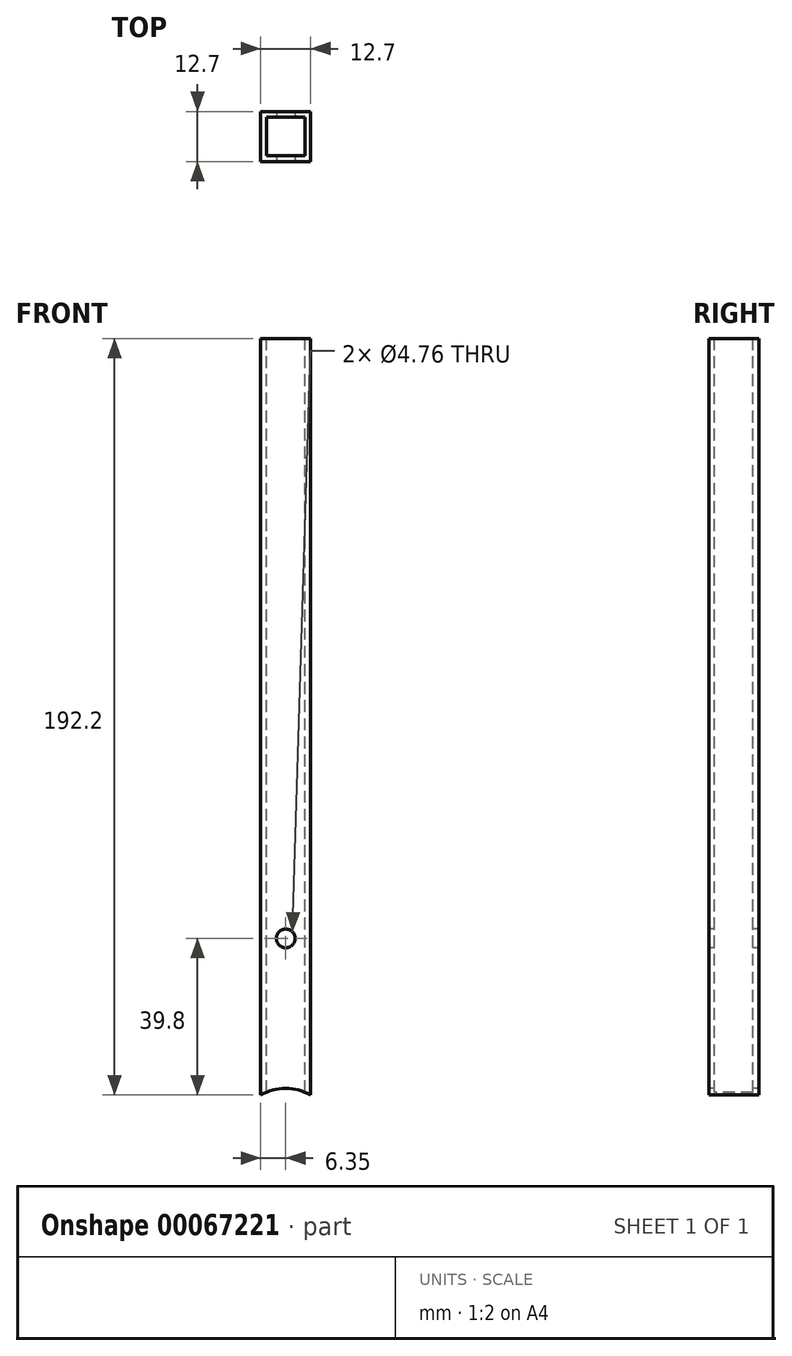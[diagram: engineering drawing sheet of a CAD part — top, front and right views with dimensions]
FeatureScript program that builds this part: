
annotation { "Feature Type Name" : "Feature", "Feature Type Description" : "" }
export const myFeature = defineFeature(function(context is Context, id is Id, definition is map)
    precondition{}
    {
        {
            var Q0;
            Q0=qCreatedBy(makeId("Top.planeOp"),FACE);
            var sketch = newSketch(context, id + "F0", { "sketchPlane" : qUnion([Q0])});
            skLineSegment(sketch, "E0.bottom", {"start": v(0, 0) * mm, "end": v(12.7, 0) * mm});
            skLineSegment(sketch, "E0.top", {"start": v(0, 12.7) * mm, "end": v(12.7, 12.7) * mm});
            skLineSegment(sketch, "E0.left", {"start": v(0, 0) * mm, "end": v(0, 12.7) * mm});
            skLineSegment(sketch, "E0.right", {"start": v(12.7, 0) * mm, "end": v(12.7, 12.7) * mm});
            skSolve(sketch);
        }
        {
            var Q0;
            Q0=makeQuery(id+"F0.imprint","IMPRINT",FACE,{"disambiguationData":[TD([[makeQuery(id+"F0.imprint","IMPRINT",EDGE,{"derivedFrom":sQuery(id+"F0.wireOp",EDGE,"E0.bottom")}),1.0]])]});
            extrude(context, id + "F1", {"entities" : qUnion([Q0]), "depth" : 203.2 * mm});
        }
        {
            var Q0;
            Q0=makeQuery(id+"F1.opExtrude","SWEPT_FACE",FACE,{"disambiguationData":[OSD([sQuery(id+"F0.wireOp",EDGE,"E0.bottom")])]});
            var sketch = newSketch(context, id + "F2", { "sketchPlane" : qUnion([Q0])});
            skCircle(sketch, "E1", {"center": v(6.35, 0) * mm, "radius": 12.7 * mm});
            skSolve(sketch);
        }
        {
            var Q0;
            {var subQ1=sQuery(id+"F0.wireOp",EDGE,"E0.bottom");var subQ6=makeQuery(id+"F1.opExtrude","CAP_EDGE",EDGE,{"disambiguationData":[OSD([subQ1])],"isStart":true});Q0=makeQuery(id+"F2.imprint","IMPRINT",FACE,{"disambiguationData":[TD([[makeQuery(id+"F2.imprint","IMPRINT",EDGE,{"derivedFrom":subQ6}),-1.0]])]});}
            var Q1;
            {var subQ1=sQuery(id+"F0.wireOp",EDGE,"E0.bottom");var subQ6=makeQuery(id+"F1.opExtrude","CAP_EDGE",EDGE,{"disambiguationData":[OSD([subQ1])],"isStart":true});Q1=makeQuery(id+"F2.imprint","IMPRINT",FACE,{"disambiguationData":[TD([[makeQuery(id+"F2.imprint","IMPRINT",EDGE,{"derivedFrom":subQ6}),1.0]])]});}
            extrude(context, id + "F3", {"entities" : qUnion([Q0, Q1]), "operationType" : NewBodyOperationType.REMOVE, "oppositeDirection" : true, "depth" : 25.4 * mm});
        }
        {
            var Q0;
            Q0=makeQuery(id+"F1.opExtrude","CAP_FACE",FACE,{"disambiguationData":[OSD([sQuery(id+"F0.wireOp",EDGE,"E0.bottom"),sQuery(id+"F0.wireOp",EDGE,"E0.top"),sQuery(id+"F0.wireOp",EDGE,"E0.left"),sQuery(id+"F0.wireOp",EDGE,"E0.right")])],"isStart":false});
            var sketch = newSketch(context, id + "F4", { "sketchPlane" : qUnion([Q0])});
            skLineSegment(sketch, "E2.0", {"start": v(0, 12.7) * mm, "end": v(12.7, 12.7) * mm});
            skLineSegment(sketch, "E3.0", {"start": v(12.7, 0) * mm, "end": v(12.7, 12.7) * mm});
            skLineSegment(sketch, "E4.0", {"start": v(0, 0) * mm, "end": v(0, 12.7) * mm});
            skLineSegment(sketch, "E5.0", {"start": v(0, 0) * mm, "end": v(12.7, 0) * mm});
            skLineSegment(sketch, "E6.bottom", {"start": v(1.45, 1.45) * mm, "end": v(11.25, 1.45) * mm});
            skLineSegment(sketch, "E6.top", {"start": v(1.45, 11.25) * mm, "end": v(11.25, 11.25) * mm});
            skLineSegment(sketch, "E6.left", {"start": v(1.45, 1.45) * mm, "end": v(1.45, 11.25) * mm});
            skLineSegment(sketch, "E6.right", {"start": v(11.25, 1.45) * mm, "end": v(11.25, 11.25) * mm});
            skLineSegment(sketch, "E7", {"start": v(1.45, 11.25) * mm, "end": v(11.25, 1.45) * mm, "construction": true});
            skLineSegment(sketch, "E8", {"start": v(11.25, 11.25) * mm, "end": v(1.45, 1.45) * mm, "construction": true});
            skPoint(sketch, "E9", {"position": v(6.35, 6.35) * mm});
            skLineSegment(sketch, "E10", {"start": v(0, 12.7) * mm, "end": v(12.7, 0) * mm, "construction": true});
            skLineSegment(sketch, "E11", {"start": v(0, 0) * mm, "end": v(12.7, 12.7) * mm, "construction": true});
            skSolve(sketch);
        }
        {
            var Q0;
            Q0=makeQuery(id+"F4.imprint","IMPRINT",FACE,{"disambiguationData":[TD([[makeQuery(id+"F4.imprint","IMPRINT",EDGE,{"derivedFrom":sQuery(id+"F4.wireOp",EDGE,"E6.bottom")}),1.0]])]});
            extrude(context, id + "F5", {"entities" : qUnion([Q0]), "operationType" : NewBodyOperationType.REMOVE, "oppositeDirection" : true, "depth" : 254 * mm});
        }
        {
            var Q0;
            Q0=makeQuery(id+"F1.opExtrude","SWEPT_FACE",FACE,{"disambiguationData":[OSD([sQuery(id+"F0.wireOp",EDGE,"E0.bottom")])]});
            var sketch = newSketch(context, id + "F6", { "sketchPlane" : qUnion([Q0])});
            skCircle(sketch, "E12", {"center": v(6.35, 50.8) * mm, "radius": 2.38 * mm});
            skSolve(sketch);
        }
        {
            var Q0;
            Q0=makeQuery(id+"F6.imprint","IMPRINT",FACE,{"disambiguationData":[TD([[makeQuery(id+"F6.imprint","IMPRINT",EDGE,{"derivedFrom":sQuery(id+"F6.wireOp",EDGE,"E12")}),1.0]])]});
            extrude(context, id + "F7", {"entities" : qUnion([Q0]), "operationType" : NewBodyOperationType.REMOVE, "oppositeDirection" : true, "depth" : 25.4 * mm});
        }
    });
